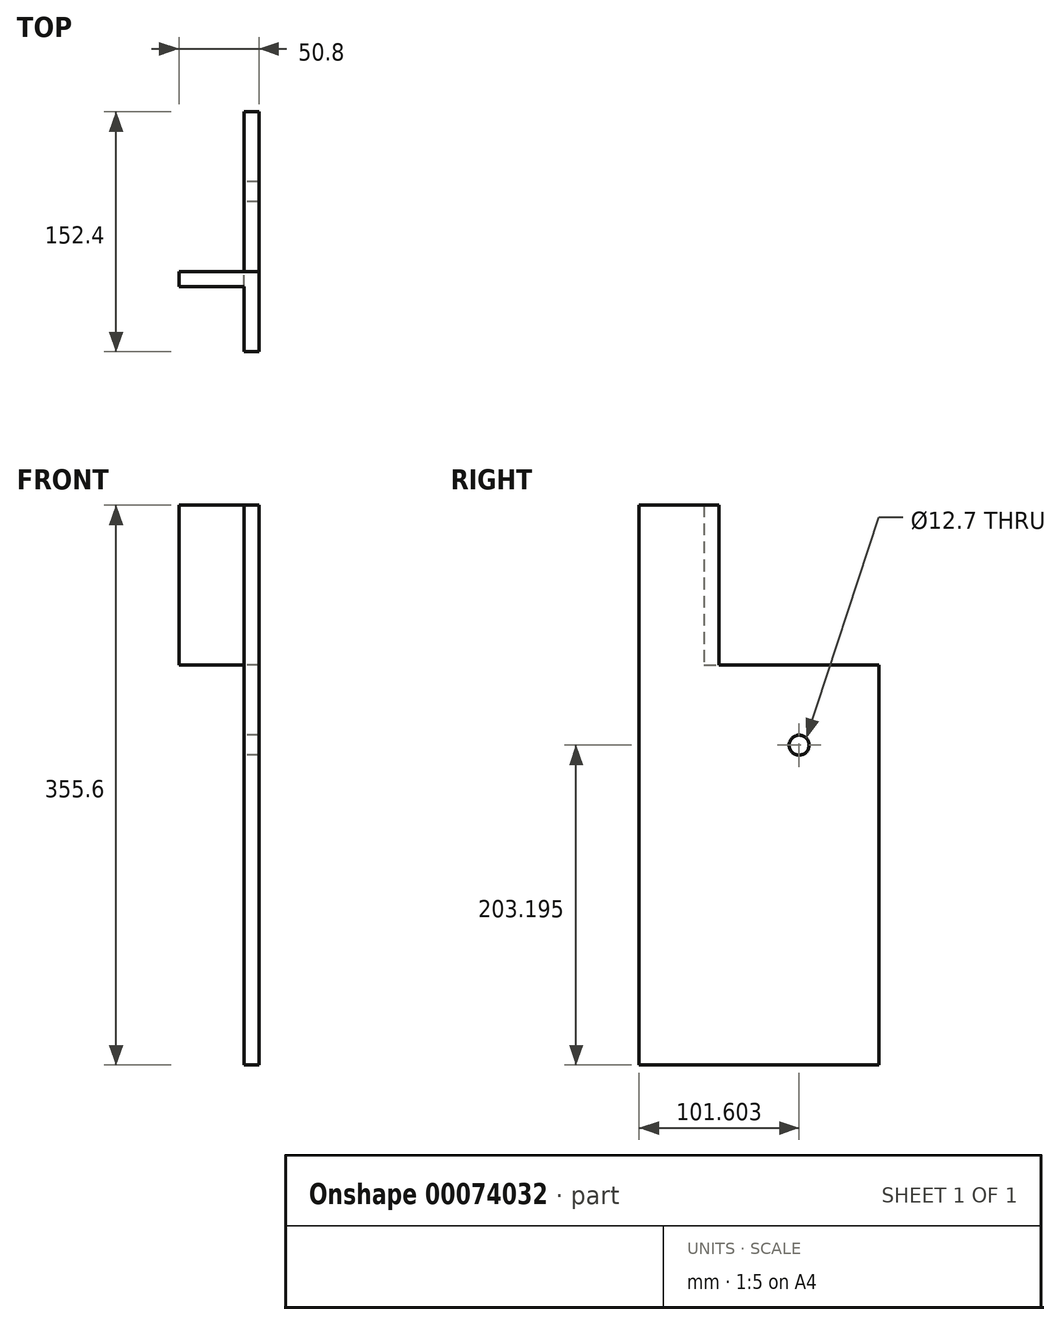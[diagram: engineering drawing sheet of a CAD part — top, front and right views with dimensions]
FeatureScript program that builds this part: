
annotation { "Feature Type Name" : "Feature", "Feature Type Description" : "" }
export const myFeature = defineFeature(function(context is Context, id is Id, definition is map)
    precondition{}
    {
        {
            var Q0;
            Q0=qCreatedBy(makeId("Right.planeOp"),FACE);
            var sketch = newSketch(context, id + "F0", { "sketchPlane" : qUnion([Q0])});
            skLineSegment(sketch, "E0.bottom", {"start": v(-58.75, -76.05) * mm, "end": v(93.65, -76.05) * mm});
            skLineSegment(sketch, "E0.top", {"start": v(-58.75, 177.95) * mm, "end": v(93.65, 177.95) * mm});
            skLineSegment(sketch, "E0.left", {"start": v(-58.75, -76.05) * mm, "end": v(-58.75, 177.95) * mm});
            skLineSegment(sketch, "E0.right", {"start": v(93.65, -76.05) * mm, "end": v(93.65, 177.95) * mm});
            skCircle(sketch, "E1", {"center": v(42.85, 127.15) * mm, "radius": 6.35 * mm});
            skSolve(sketch);
        }
        {
            var Q0;
            Q0 = qSketchRegion(id + "F0", true);
            extrude(context, id + "F1", {"entities" : qUnion([Q0]), "depth" : 9.52 * mm, "symmetric" : true});
        }
        {
            var Q0;
            Q0=makeQuery(id+"F1.opExtrude","SWEPT_FACE",FACE,{"disambiguationData":[OSD([sQuery(id+"F0.wireOp",EDGE,"E0.top")])]});
            var sketch = newSketch(context, id + "F2", { "sketchPlane" : qUnion([Q0])});
            skLineSegment(sketch, "E2", {"start": v(4.76, -58.75) * mm, "end": v(4.76, -7.95) * mm});
            skLineSegment(sketch, "E3", {"start": v(4.76, -7.95) * mm, "end": v(-46.04, -7.95) * mm});
            skLineSegment(sketch, "E4", {"start": v(-46.04, -7.95) * mm, "end": v(-46.04, -17.47) * mm});
            skLineSegment(sketch, "E5", {"start": v(-46.04, -17.47) * mm, "end": v(-4.76, -17.47) * mm});
            skLineSegment(sketch, "E6", {"start": v(-4.76, -17.47) * mm, "end": v(-4.76, -58.75) * mm});
            skLineSegment(sketch, "E7", {"start": v(-4.76, -58.75) * mm, "end": v(4.76, -58.75) * mm});
            skSolve(sketch);
        }
        {
            var Q0;
            Q0 = qSketchRegion(id + "F2", true);
            extrude(context, id + "F3", {"entities" : qUnion([Q0]), "operationType" : NewBodyOperationType.ADD, "depth" : 101.6 * mm});
        }
    });
